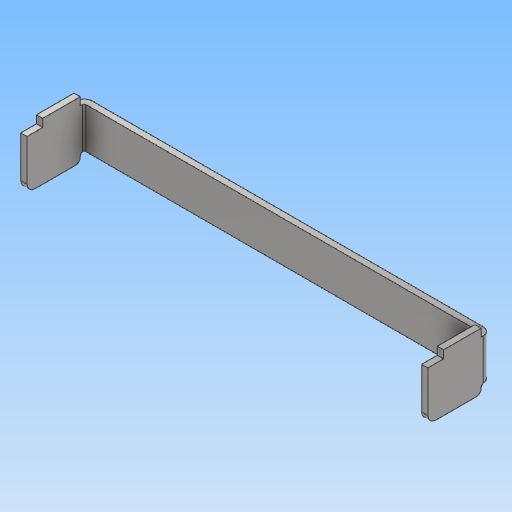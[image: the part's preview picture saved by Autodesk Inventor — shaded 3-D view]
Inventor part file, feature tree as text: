
AUTODESK INVENTOR PART (.ipt)
format: ipt  version: 2020 (Build 240168000, 168)  size: 268,288 bytes
history: native  units: mm
features: other x4, extrude x1
ambient origin geometry x8: Origin, YZ Plane, XZ Plane, XY Plane, X Axis, Y Axis, Z Axis, Center Point
bodies: Body1 (feature_tree)
feature tree (5):
  other  "實體1"
  extrude  "擠出1"  Depth=2.0mm TaperAngle=0.0deg
  other  "折彎零件1"
  other  "折彎零件2"
  other  "定義1"
